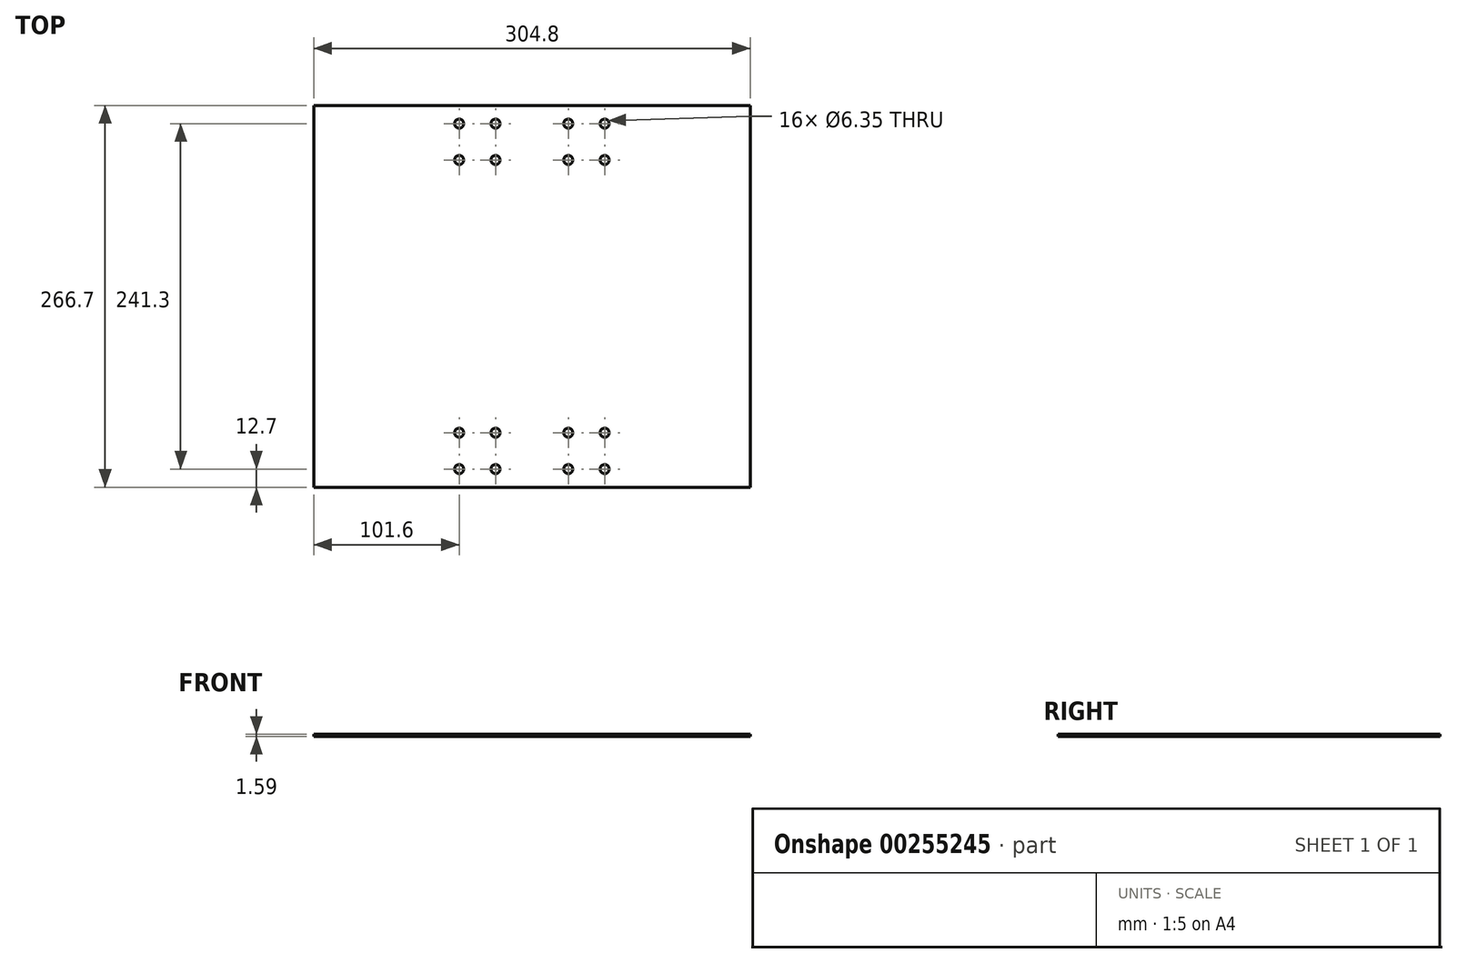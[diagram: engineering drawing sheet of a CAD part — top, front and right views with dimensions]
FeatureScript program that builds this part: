
annotation { "Feature Type Name" : "Feature", "Feature Type Description" : "" }
export const myFeature = defineFeature(function(context is Context, id is Id, definition is map)
    precondition{}
    {
        {
            var Q0;
            Q0=qCreatedBy(makeId("Top.planeOp"),FACE);
            var sketch = newSketch(context, id + "F0", { "sketchPlane" : qUnion([Q0])});
            skLineSegment(sketch, "E0.bottom", {"start": v(152.4, -133.35) * mm, "end": v(-152.4, -133.35) * mm});
            skLineSegment(sketch, "E0.top", {"start": v(152.4, 133.35) * mm, "end": v(-152.4, 133.35) * mm});
            skLineSegment(sketch, "E0.left", {"start": v(152.4, -133.35) * mm, "end": v(152.4, 133.35) * mm});
            skLineSegment(sketch, "E0.right", {"start": v(-152.4, -133.35) * mm, "end": v(-152.4, 133.35) * mm});
            skPoint(sketch, "E0.middle", {"position": v(0, 0) * mm});
            skLineSegment(sketch, "E1", {"start": v(0, 133.35) * mm, "end": v(0, -133.35) * mm, "construction": true});
            skLineSegment(sketch, "E2.bottom", {"start": v(-25.4, -120.65) * mm, "end": v(-50.8, -120.65) * mm, "construction": true});
            skLineSegment(sketch, "E2.top", {"start": v(-25.4, -95.25) * mm, "end": v(-50.8, -95.25) * mm, "construction": true});
            skLineSegment(sketch, "E2.left", {"start": v(-25.4, -120.65) * mm, "end": v(-25.4, -95.25) * mm, "construction": true});
            skLineSegment(sketch, "E2.right", {"start": v(-50.8, -120.65) * mm, "end": v(-50.8, -95.25) * mm, "construction": true});
            skPoint(sketch, "E2.middle", {"position": v(-38.1, -107.95) * mm});
            skLineSegment(sketch, "E3", {"start": v(-152.4, 0) * mm, "end": v(152.4, 0) * mm, "construction": true});
            skCircle(sketch, "E4", {"center": v(-50.8, -95.25) * mm, "radius": 3.18 * mm});
            skCircle(sketch, "E5", {"center": v(-25.4, -95.25) * mm, "radius": 3.18 * mm});
            skCircle(sketch, "E6", {"center": v(-25.4, -120.65) * mm, "radius": 3.18 * mm});
            skCircle(sketch, "E7", {"center": v(-50.8, -120.65) * mm, "radius": 3.18 * mm});
            skCircle(sketch, "E8.MirrorC", {"center": v(50.8, -95.25) * mm, "radius": 3.18 * mm});
            skCircle(sketch, "E9.MirrorC", {"center": v(25.4, -95.25) * mm, "radius": 3.18 * mm});
            skCircle(sketch, "E10.MirrorC", {"center": v(25.4, -120.65) * mm, "radius": 3.18 * mm});
            skCircle(sketch, "E11.MirrorC", {"center": v(50.8, -120.65) * mm, "radius": 3.18 * mm});
            skCircle(sketch, "E12.MirrorC", {"center": v(-50.8, 95.25) * mm, "radius": 3.18 * mm});
            skCircle(sketch, "E13.MirrorC", {"center": v(-25.4, 95.25) * mm, "radius": 3.18 * mm});
            skCircle(sketch, "E14.MirrorC", {"center": v(25.4, 95.25) * mm, "radius": 3.18 * mm});
            skCircle(sketch, "E15.MirrorC", {"center": v(50.8, 95.25) * mm, "radius": 3.18 * mm});
            skCircle(sketch, "E16.MirrorC", {"center": v(50.8, 120.65) * mm, "radius": 3.18 * mm});
            skCircle(sketch, "E17.MirrorC", {"center": v(25.4, 120.65) * mm, "radius": 3.18 * mm});
            skCircle(sketch, "E18.MirrorC", {"center": v(-25.4, 120.65) * mm, "radius": 3.18 * mm});
            skCircle(sketch, "E19.MirrorC", {"center": v(-50.8, 120.65) * mm, "radius": 3.18 * mm});
            skSolve(sketch);
        }
        {
            var Q0;
            Q0=makeQuery(id+"F0.imprint","IMPRINT",FACE,{"disambiguationData":[TD([[makeQuery(id+"F0.imprint","IMPRINT",EDGE,{"derivedFrom":sQuery(id+"F0.wireOp",EDGE,"E0.bottom")}),-1.0]])]});
            extrude(context, id + "F1", {"entities" : qUnion([Q0]), "depth" : 1.59 * mm});
        }
    });
